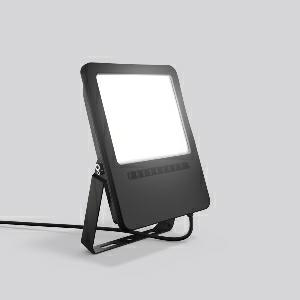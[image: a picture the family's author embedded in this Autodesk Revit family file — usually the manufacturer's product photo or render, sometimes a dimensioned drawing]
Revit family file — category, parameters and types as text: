
# Revit family: hb_450_722126_003_56d3
name_source: partatom
category: Lighting Fixtures
units: mm (PartAtom-declared; Revit-internal decimal feet)

## family parameters
Cut with Voids When Loaded = No
Host = Face
Light Source = No
Part Type = Normal
Room Calculation Point = No
Round Connector Dimension = Use Diameter
Shared = No

## types (1)
- HB 450 (1 x LED Modul 840, 11000 lm, 4000)
    Apparent Load = 100 VA
    CIE Flux Codes = 51 85 99 100 100
    Color Rendering = 80
    Color Temperature = 4000
    Default Elevation = 1800 mm
    Description = Series: HB 450
Projector for direct mains connection. Housing: die-cast aluminium, powder-coated. Bracket: steel, powder-coated. Clear glass cover. Wide flood. Pre-wired with 500 mm connection cable. 
Colour: black
Length: 360 mm
Width: 240 mm
Height: 48 mm
Lamp: LED
System power: 100 W
Rated luminous flux: 11000 lm
Luminous efficiency: 110 lm/W
Control gear: Regulated power supply
Protection class: I
Type of protection: IP 65
    Height = 48 mm  [stored 0.15748 ft]
    Lamp = 1 x LED Modul 840
    Lamp Light Flux = 11000 lm
    Lamp count = 1
    Length = 360 mm
    Lifetime = 50000 h
    Luminous efficacy = 110 lm/W
    Manufacturer = RZB
    ModVariant = No
    Model = 722126.003
    Mounting Place = Floor
    Mounting Type = Surface mounted
    Number of Poles = 1
    OnlyDefault = Yes
    Power Factor = 1
    Product Name = HB 450
    Product group = Floodlights and spotlights
    ProductGroupID = 1354
    Protection Class = Protection class I
    Protection Degree = IP 65
    RLX_Detail_Level = 1
    RLX_Emergency_Light_Flux = 0 lm
    RLX_Emergency_Type = 0
    RLX_Emergency_Type_DB = No
    RlxData = <blob elided: 27481 chars, md5=d2471cb1>
    Socket = socket
    Standby Power = 0 W
    System Light Flux = 11000 lm
    System Power = 100 W
    Type Comments = Product without accessories
    Type Image = 722125.003.jpg
    URL = http://relux.com
    VarID = ---
    Voltage = 230 V
    Voltage Range = 220-240 V
    Weight = 0.00 kg
    Width = 240 mm

note: [stored X ft] marks values corroborated as IEEE doubles in the binary element streams (Revit-internal decimal feet)

## geometry (parser evidence)
native form markers: Blend x4, Sweep x12
no freeform markers — native parametric forms only
